# Revit family: Dallmeier_Dome_Cameras_en
name_source: partatom
category: Sicherheitsgeräte
units: mm (PartAtom-declared; Revit-internal decimal feet)

## family parameters
Basisbauteil = Fläche
Beim Laden mit Abzugskörper schneiden = Nein
Bemaßung runder Anschluss = Durchmesser verwenden
Beschriftungsausrichtung beibehalten = Nein
Gemeinsam genutzt = Nein
Raumberechnungspunkt = Nein
Teiletyp = Normal

## types (12) — shared parameters
Hersteller = Dallmeier electronic GmbH
URL = https://www.dallmeier.com
Vorgabe-Ansicht = 122 cm
number of sensors = 1
operating temperature = −20°C to +50°C

## per-type parameters (varying)
| type | 4:3 Available | Dome_6000 | Dome_HDV | Long Horizontal FOV | Modell | Pixel Horizontal 16:9 | Pixel Horizontal 4:3 | Short Horizontal FOV | dimensions | power consumption | voltage supply | weight |
| DDF Ultraline 5450 HDV-DN 4-10mm | Ja | Nein | Ja | 105,00° | Dallmeier Dome DDF 5450 4-10mm | 3840 | 4000 | 42,00° | Ø170x135mm / Ø152x136mm | 12 W | 24 V | 1,20 kg |
| DDF Ultraline 5450 HDV-DN 12-50mm | Ja | Nein | Ja | 34,00° | Dallmeier Dome DDF 5450 12-50mm | 3840 | 4000 | 8,80° | Ø170x135mm / Ø152x136mm | 12 W | 24 V | 1,20 kg |
| DDF Nightline 5250 HDV-DN 4,5-10mm | Ja | Nein | Ja | 87,00° | Dallmeier Dome DDF 5250 4,5-10mm | 1920 | 1440 | 40,00° | Ø170x135mm / Ø152x136mm | 6 W | 24 V | 1,20 kg |
| DDF Nightline 5250 HDV-DN 12-40mm | Ja | Nein | Ja | 35,00° | Dallmeier Dome DDF 5250 12-40mm | 1920 | 1440 | 11,00° | Ø170x135mm / Ø152x136mm | 6 W | 24 V | 1,20 kg |
| DDF Primeline 5120 HDV-DN 3-10mm | Ja | Nein | Ja | 111,00° | Dallmeier Dome DDF 5120 3-10mm | 1920 | 1440 | 31,90° | Ø170x135mm / Ø152x133mm / Ø149x124mm | 6 W | 12 V | 1,20 kg |
| DDF Primeline 5120 HDV-DN 12-40mm | Ja | Nein | Ja | 23,80° | Dallmeier Dome DDF 5120 12-40mm | 1920 | 1440 | 8,30° | Ø170x135mm / Ø152x133mm / Ø149x124mm | 6 W | 12 V | 1,20 kg |
| DDF Primeline 5140 HDV-DN 3-10mm | Ja | Nein | Ja | 111,00° | Dallmeier Dome DDF 5140 3-10mm | 2592 | 2592 | 31,90° | Ø170x135mm / Ø152x133mm / Ø149x124mm | 6 W | 12 V | 1,20 kg |
| DDF Primeline 5140 HDV-DN 12-40mm | Ja | Nein | Ja | 23,80° | Dallmeier Dome DDF 5140 12-40mm | 2592 | 2592 | 8,30° | Ø170x135mm / Ø152x133mm / Ø149x124mm | 6 W | 12 V | 1,20 kg |
| Domera RDF 6400 DN 4,5-9,7mm | Nein | Ja | Nein | 112,00° | Dallmeier Domera RDF 6400 DN 4,5-9,7mm | 2688 | 2688 | 46,00° | Ø171x133mm / Ø171x137mm | 12 W | 24 V | 1,40 kg |
| Domera RDF 6400 DN 12-40mm | Nein | Ja | Nein | 34,00° | Dallmeier Domera RDF 6400 DN 12-40mm | 2688 | 2688 | 11,00° | Ø171x133mm / Ø171x137mm | 12 W | 24 V | 1,40 kg |
| Domera RDF 6800 DN 4,5-9,7mm | Nein | Ja | Nein | 112,00° | Dallmeier Domera RDF 6800 DN 4,5-9,7mm | 3840 | 4000 | 46,00° | Ø171x133mm / Ø171x137mm | 12 W | 24 V | 1,40 kg |
| Domera RDF 6800 DN 12-40mm | Nein | Ja | Nein | 34,00° | Dallmeier Domera RDF 6800 DN 12-40mm | 3840 | 4000 | 11,00° | Ø171x133mm / Ø171x137mm | 12 W | 24 V | 1,40 kg |

## geometry (parser evidence)
native form markers: Sweep x42
no freeform markers — native parametric forms only
